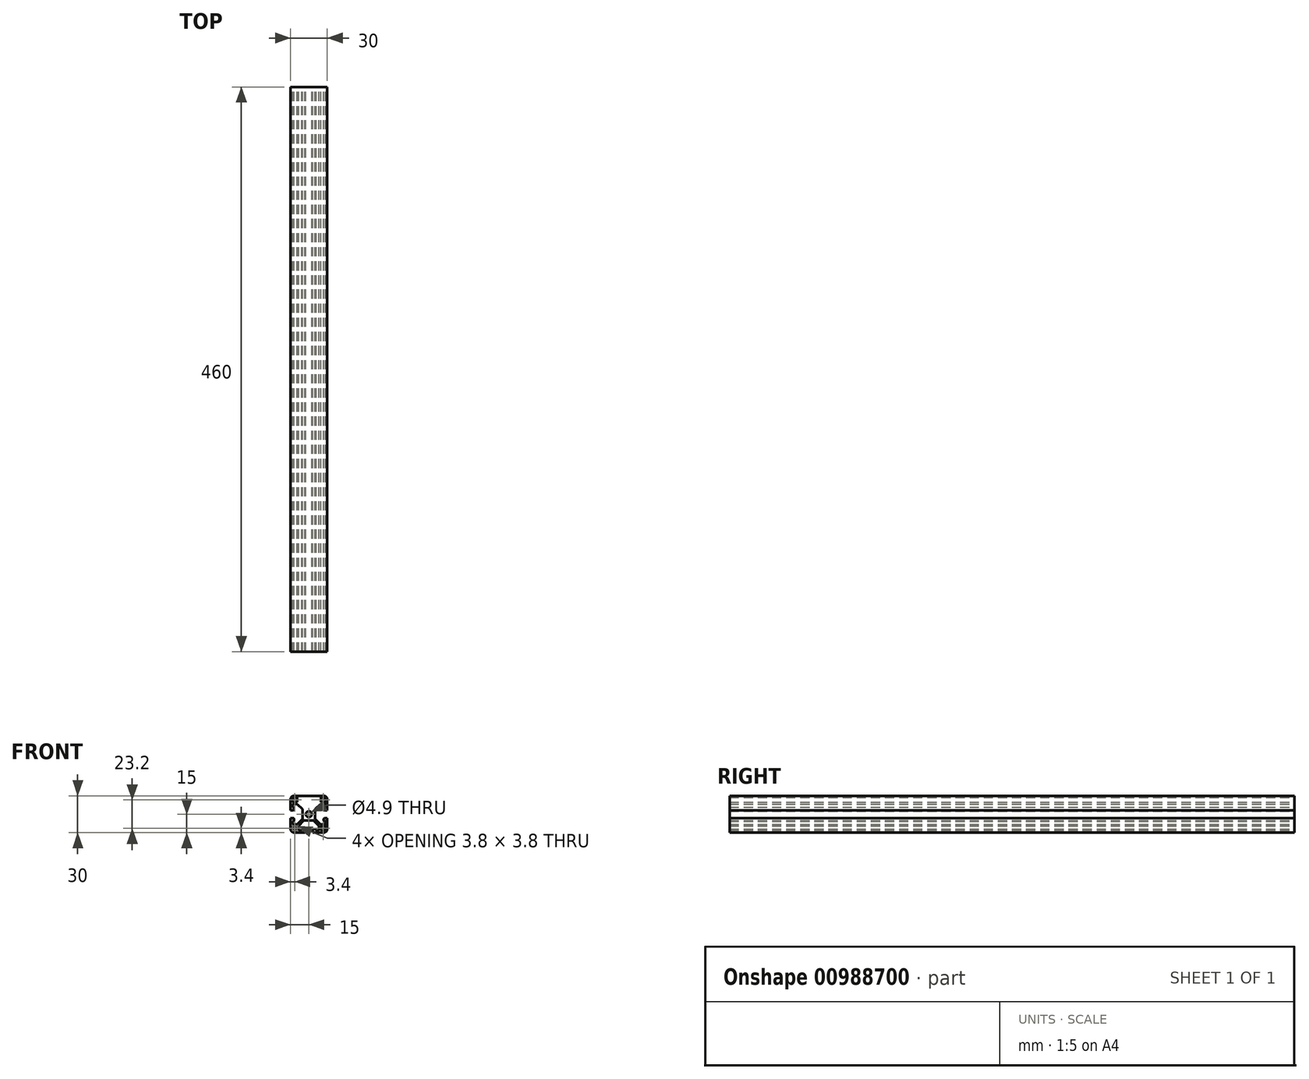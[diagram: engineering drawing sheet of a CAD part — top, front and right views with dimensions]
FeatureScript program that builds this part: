
annotation { "Feature Type Name" : "Feature", "Feature Type Description" : "" }
export const myFeature = defineFeature(function(context is Context, id is Id, definition is map)
    precondition{}
    {
        {
            var Q0;
            Q0=qCreatedBy(makeId("Front.planeOp"),FACE);
            var sketch = newSketch(context, id + "F0", { "sketchPlane" : qUnion([Q0])});
            skLineSegment(sketch, "E0.bottom", {"start": v(-12, 15) * mm, "end": v(12, 15) * mm});
            skLineSegment(sketch, "E0.top", {"start": v(-12, -15) * mm, "end": v(12, -15) * mm});
            skLineSegment(sketch, "E0.left", {"start": v(-15, 12) * mm, "end": v(-15, -12) * mm});
            skLineSegment(sketch, "E0.right", {"start": v(15, 12) * mm, "end": v(15, -12) * mm});
            skPoint(sketch, "E1.visualSharp", {"position": v(-15, 15) * mm});
            skArc(sketch, "E1.filletArc", {"start": v(-12, 15) * mm, "mid": v(-14.12, 14.12) * mm, "end": v(-15, 12) * mm});
            skPoint(sketch, "E2.visualSharp", {"position": v(15, 15) * mm});
            skArc(sketch, "E2.filletArc", {"start": v(15, 12) * mm, "mid": v(14.12, 14.12) * mm, "end": v(12, 15) * mm});
            skPoint(sketch, "E3.visualSharp", {"position": v(15, -15) * mm});
            skArc(sketch, "E3.filletArc", {"start": v(12, -15) * mm, "mid": v(14.12, -14.12) * mm, "end": v(15, -12) * mm});
            skPoint(sketch, "E4.visualSharp", {"position": v(-15, -15) * mm});
            skArc(sketch, "E4.filletArc", {"start": v(-15, -12) * mm, "mid": v(-14.12, -14.12) * mm, "end": v(-12, -15) * mm});
            skCircle(sketch, "E5", {"center": v(0, 0) * mm, "radius": 2.45 * mm});
            skPoint(sketch, "E6", {"position": v(15, 8.22) * mm});
            skPoint(sketch, "E7", {"position": v(15, -8.22) * mm});
            skPoint(sketch, "E8", {"position": v(15, 3.17) * mm});
            skPoint(sketch, "E9", {"position": v(15, -3.18) * mm});
            skLineSegment(sketch, "E10", {"start": v(15, 3.17) * mm, "end": v(13.09, 3.17) * mm});
            skLineSegment(sketch, "E11", {"start": v(13.09, -3.18) * mm, "end": v(15, -3.18) * mm});
            skPoint(sketch, "E12", {"position": v(12.06, -5.83) * mm});
            skPoint(sketch, "E13", {"position": v(12.06, 5.82) * mm});
            skPoint(sketch, "E14", {"position": v(13.5, -5.82) * mm});
            skPoint(sketch, "E15", {"position": v(13.5, 5.82) * mm});
            skPoint(sketch, "E16", {"position": v(13.5, 8.22) * mm});
            skPoint(sketch, "E17", {"position": v(13.5, -8.22) * mm});
            skPoint(sketch, "E18", {"position": v(9.5, 8.22) * mm});
            skPoint(sketch, "E19", {"position": v(9.5, -8.22) * mm});
            skPoint(sketch, "E20", {"position": v(5.1, -3.92) * mm});
            skPoint(sketch, "E21", {"position": v(5.1, 4.08) * mm});
            skLineSegment(sketch, "E22", {"start": v(12.09, -4.16) * mm, "end": v(12.08, -4.81) * mm});
            skLineSegment(sketch, "E23", {"start": v(13.5, -5.82) * mm, "end": v(13.5, -8.22) * mm});
            skLineSegment(sketch, "E24", {"start": v(9.2, -7.94) * mm, "end": v(5.4, -4.21) * mm});
            skLineSegment(sketch, "E25", {"start": v(5.1, 3.65) * mm, "end": v(5.1, -3.5) * mm});
            skLineSegment(sketch, "E26", {"start": v(5.41, 4.38) * mm, "end": v(9.21, 7.95) * mm});
            skLineSegment(sketch, "E27", {"start": v(13.5, 8.22) * mm, "end": v(9.9, 8.22) * mm});
            skLineSegment(sketch, "E28", {"start": v(13.5, 8.22) * mm, "end": v(13.5, 5.82) * mm});
            skLineSegment(sketch, "E29", {"start": v(13.08, 5.82) * mm, "end": v(13.5, 5.82) * mm});
            skLineSegment(sketch, "E30", {"start": v(12.08, 4.81) * mm, "end": v(12.09, 4.16) * mm});
            skLineSegment(sketch, "E31", {"start": v(13.08, -5.83) * mm, "end": v(13.5, -5.83) * mm});
            skLineSegment(sketch, "E32", {"start": v(13.5, -8.22) * mm, "end": v(9.9, -8.22) * mm});
            skLineSegment(sketch, "E33", {"start": v(13.5, -8.22) * mm, "end": v(13.5, -5.82) * mm});
            skArc(sketch, "E34.filletArc", {"start": v(9.9, 8.22) * mm, "mid": v(9.53, 8.15) * mm, "end": v(9.21, 7.95) * mm});
            skArc(sketch, "E35.filletArc", {"start": v(5.41, 4.38) * mm, "mid": v(5.18, 4.04) * mm, "end": v(5.1, 3.65) * mm});
            skArc(sketch, "E36.filletArc", {"start": v(5.1, -3.5) * mm, "mid": v(5.18, -3.89) * mm, "end": v(5.4, -4.21) * mm});
            skArc(sketch, "E37.filletArc", {"start": v(9.2, -7.94) * mm, "mid": v(9.53, -8.15) * mm, "end": v(9.9, -8.22) * mm});
            skArc(sketch, "E38.filletArc", {"start": v(12.08, -4.81) * mm, "mid": v(12.36, -5.53) * mm, "end": v(13.08, -5.83) * mm});
            skPoint(sketch, "E39.visualSharp", {"position": v(12.1, -3.18) * mm});
            skArc(sketch, "E39.filletArc", {"start": v(13.09, -3.18) * mm, "mid": v(12.38, -3.46) * mm, "end": v(12.09, -4.16) * mm});
            skPoint(sketch, "E40.visualSharp", {"position": v(12.1, 3.17) * mm});
            skArc(sketch, "E40.filletArc", {"start": v(12.09, 4.16) * mm, "mid": v(12.38, 3.46) * mm, "end": v(13.09, 3.17) * mm});
            skArc(sketch, "E41.filletArc", {"start": v(13.08, 5.82) * mm, "mid": v(12.36, 5.53) * mm, "end": v(12.08, 4.81) * mm});
            skArc(sketch, "E42.MirrorCS", {"start": v(-5.1, -3.5) * mm, "mid": v(-5.18, -3.89) * mm, "end": v(-5.4, -4.21) * mm});
            skLineSegment(sketch, "E43.MirrorCS", {"start": v(-13.08, -5.83) * mm, "end": v(-13.5, -5.83) * mm});
            skArc(sketch, "E44.MirrorCS", {"start": v(-9.2, -7.94) * mm, "mid": v(-9.53, -8.15) * mm, "end": v(-9.9, -8.22) * mm});
            skLineSegment(sketch, "E45.MirrorCS", {"start": v(-13.08, 5.82) * mm, "end": v(-13.5, 5.82) * mm});
            skArc(sketch, "E46.MirrorCS", {"start": v(-5.41, 4.38) * mm, "mid": v(-5.18, 4.04) * mm, "end": v(-5.1, 3.65) * mm});
            skArc(sketch, "E47.MirrorCS", {"start": v(-9.9, 8.22) * mm, "mid": v(-9.53, 8.15) * mm, "end": v(-9.21, 7.95) * mm});
            skArc(sketch, "E48.MirrorCS", {"start": v(-13.08, 5.82) * mm, "mid": v(-12.36, 5.53) * mm, "end": v(-12.08, 4.81) * mm});
            skLineSegment(sketch, "E49.MirrorCS", {"start": v(-12.08, 4.81) * mm, "end": v(-12.09, 4.16) * mm});
            skLineSegment(sketch, "E50.MirrorCS", {"start": v(-12.09, -4.16) * mm, "end": v(-12.08, -4.81) * mm});
            skArc(sketch, "E51.MirrorCS", {"start": v(-12.08, -4.81) * mm, "mid": v(-12.36, -5.53) * mm, "end": v(-13.08, -5.83) * mm});
            skLineSegment(sketch, "E52.MirrorCS", {"start": v(-13.5, -8.22) * mm, "end": v(-13.5, -5.82) * mm});
            skLineSegment(sketch, "E53.MirrorCS", {"start": v(-13.5, -5.82) * mm, "end": v(-13.5, -8.22) * mm});
            skLineSegment(sketch, "E54.MirrorCS", {"start": v(-13.09, -3.18) * mm, "end": v(-15, -3.18) * mm});
            skArc(sketch, "E55.MirrorCS", {"start": v(-12.09, 4.16) * mm, "mid": v(-12.38, 3.46) * mm, "end": v(-13.09, 3.17) * mm});
            skArc(sketch, "E56.MirrorCS", {"start": v(-13.09, -3.18) * mm, "mid": v(-12.38, -3.46) * mm, "end": v(-12.09, -4.16) * mm});
            skLineSegment(sketch, "E57.MirrorCS", {"start": v(-15, 3.17) * mm, "end": v(-13.09, 3.17) * mm});
            skPoint(sketch, "E58.MirrorP", {"position": v(-5.1, -3.92) * mm});
            skPoint(sketch, "E59.MirrorP", {"position": v(-9.5, -8.22) * mm});
            skPoint(sketch, "E60.MirrorP", {"position": v(-13.5, -8.22) * mm});
            skPoint(sketch, "E61.MirrorP", {"position": v(-12.06, 5.82) * mm});
            skPoint(sketch, "E62.MirrorP", {"position": v(-5.1, 4.08) * mm});
            skLineSegment(sketch, "E63.MirrorCS", {"start": v(-13.5, 8.22) * mm, "end": v(-13.5, 5.82) * mm});
            skPoint(sketch, "E64.MirrorP", {"position": v(-12.06, -5.83) * mm});
            skPoint(sketch, "E65.MirrorP", {"position": v(-9.5, 8.22) * mm});
            skPoint(sketch, "E66.MirrorP", {"position": v(-15, 8.22) * mm});
            skPoint(sketch, "E67.MirrorP", {"position": v(-13.5, 5.82) * mm});
            skLineSegment(sketch, "E68.MirrorCS", {"start": v(-13.5, 8.22) * mm, "end": v(-9.9, 8.22) * mm});
            skPoint(sketch, "E69.MirrorP", {"position": v(-13.5, -5.82) * mm});
            skLineSegment(sketch, "E70.MirrorCS", {"start": v(-13.5, -8.22) * mm, "end": v(-9.9, -8.22) * mm});
            skLineSegment(sketch, "E71.MirrorCS", {"start": v(-5.1, 3.65) * mm, "end": v(-5.1, -3.5) * mm});
            skPoint(sketch, "E72.MirrorP", {"position": v(-13.5, 8.22) * mm});
            skPoint(sketch, "E73.MirrorP", {"position": v(-15, -3.18) * mm});
            skPoint(sketch, "E74.MirrorP", {"position": v(-12.1, 3.17) * mm});
            skPoint(sketch, "E75.MirrorP", {"position": v(-15, -8.22) * mm});
            skPoint(sketch, "E76.MirrorP", {"position": v(-12.1, -3.18) * mm});
            skLineSegment(sketch, "E77.MirrorCS", {"start": v(-5.41, 4.38) * mm, "end": v(-9.21, 7.95) * mm});
            skLineSegment(sketch, "E78.MirrorCS", {"start": v(-9.2, -7.94) * mm, "end": v(-5.4, -4.21) * mm});
            skPoint(sketch, "E79.MirrorP", {"position": v(-15, 3.17) * mm});
            skArc(sketch, "E80.MirrorCS", {"start": v(-3.5, 5.1) * mm, "mid": v(-3.89, 5.18) * mm, "end": v(-4.21, 5.4) * mm});
            skLineSegment(sketch, "E81.MirrorCS", {"start": v(-5.82, 13.08) * mm, "end": v(-5.82, 13.5) * mm});
            skArc(sketch, "E82.MirrorCS", {"start": v(-7.94, 9.2) * mm, "mid": v(-8.15, 9.53) * mm, "end": v(-8.22, 9.9) * mm});
            skLineSegment(sketch, "E83.MirrorCS", {"start": v(5.83, 13.08) * mm, "end": v(5.83, 13.5) * mm});
            skArc(sketch, "E84.MirrorCS", {"start": v(4.38, 5.41) * mm, "mid": v(4.04, 5.18) * mm, "end": v(3.65, 5.1) * mm});
            skArc(sketch, "E85.MirrorCS", {"start": v(8.23, 9.9) * mm, "mid": v(8.15, 9.53) * mm, "end": v(7.95, 9.21) * mm});
            skArc(sketch, "E86.MirrorCS", {"start": v(5.83, 13.08) * mm, "mid": v(5.53, 12.36) * mm, "end": v(4.81, 12.08) * mm});
            skLineSegment(sketch, "E87.MirrorCS", {"start": v(4.81, 12.08) * mm, "end": v(4.16, 12.09) * mm});
            skLineSegment(sketch, "E88.MirrorCS", {"start": v(-4.16, 12.09) * mm, "end": v(-4.81, 12.08) * mm});
            skArc(sketch, "E89.MirrorCS", {"start": v(-4.81, 12.08) * mm, "mid": v(-5.53, 12.36) * mm, "end": v(-5.82, 13.08) * mm});
            skLineSegment(sketch, "E90.MirrorCS", {"start": v(-8.22, 13.5) * mm, "end": v(-5.82, 13.5) * mm});
            skLineSegment(sketch, "E91.MirrorCS", {"start": v(-5.82, 13.5) * mm, "end": v(-8.22, 13.5) * mm});
            skLineSegment(sketch, "E92.MirrorCS", {"start": v(-3.17, 13.09) * mm, "end": v(-3.17, 15) * mm});
            skArc(sketch, "E93.MirrorCS", {"start": v(4.16, 12.09) * mm, "mid": v(3.46, 12.38) * mm, "end": v(3.18, 13.09) * mm});
            skArc(sketch, "E94.MirrorCS", {"start": v(-3.17, 13.09) * mm, "mid": v(-3.46, 12.38) * mm, "end": v(-4.16, 12.09) * mm});
            skLineSegment(sketch, "E95.MirrorCS", {"start": v(3.18, 15) * mm, "end": v(3.18, 13.09) * mm});
            skPoint(sketch, "E96.MirrorP", {"position": v(-3.92, 5.1) * mm});
            skPoint(sketch, "E97.MirrorP", {"position": v(-8.22, 9.5) * mm});
            skPoint(sketch, "E98.MirrorP", {"position": v(-8.22, 13.5) * mm});
            skPoint(sketch, "E99.MirrorP", {"position": v(5.83, 12.06) * mm});
            skPoint(sketch, "E100.MirrorP", {"position": v(4.08, 5.1) * mm});
            skLineSegment(sketch, "E101.MirrorCS", {"start": v(8.23, 13.5) * mm, "end": v(5.83, 13.5) * mm});
            skPoint(sketch, "E102.MirrorP", {"position": v(-5.82, 12.06) * mm});
            skPoint(sketch, "E103.MirrorP", {"position": v(8.23, 9.5) * mm});
            skPoint(sketch, "E104.MirrorP", {"position": v(8.23, 15) * mm});
            skPoint(sketch, "E105.MirrorP", {"position": v(5.83, 13.5) * mm});
            skLineSegment(sketch, "E106.MirrorCS", {"start": v(8.23, 13.5) * mm, "end": v(8.23, 9.9) * mm});
            skPoint(sketch, "E107.MirrorP", {"position": v(-5.82, 13.5) * mm});
            skLineSegment(sketch, "E108.MirrorCS", {"start": v(-8.22, 13.5) * mm, "end": v(-8.22, 9.9) * mm});
            skLineSegment(sketch, "E109.MirrorCS", {"start": v(3.65, 5.1) * mm, "end": v(-3.5, 5.1) * mm});
            skPoint(sketch, "E110.MirrorP", {"position": v(8.23, 13.5) * mm});
            skPoint(sketch, "E111.MirrorP", {"position": v(-3.17, 15) * mm});
            skPoint(sketch, "E112.MirrorP", {"position": v(3.18, 12.1) * mm});
            skPoint(sketch, "E113.MirrorP", {"position": v(-8.22, 15) * mm});
            skPoint(sketch, "E114.MirrorP", {"position": v(-3.17, 12.1) * mm});
            skLineSegment(sketch, "E115.MirrorCS", {"start": v(4.38, 5.41) * mm, "end": v(7.95, 9.21) * mm});
            skLineSegment(sketch, "E116.MirrorCS", {"start": v(-7.94, 9.2) * mm, "end": v(-4.21, 5.4) * mm});
            skPoint(sketch, "E117.MirrorP", {"position": v(3.18, 15) * mm});
            skPoint(sketch, "E118", {"position": v(-8.22, -15) * mm});
            skArc(sketch, "E119.MirrorCS", {"start": v(3.5, -5.1) * mm, "mid": v(3.89, -5.18) * mm, "end": v(4.21, -5.4) * mm});
            skLineSegment(sketch, "E120.MirrorCS", {"start": v(5.83, -13.08) * mm, "end": v(5.83, -13.5) * mm});
            skArc(sketch, "E121.MirrorCS", {"start": v(7.94, -9.2) * mm, "mid": v(8.15, -9.53) * mm, "end": v(8.23, -9.9) * mm});
            skLineSegment(sketch, "E122.MirrorCS", {"start": v(-5.82, -13.08) * mm, "end": v(-5.82, -13.5) * mm});
            skArc(sketch, "E123.MirrorCS", {"start": v(-4.38, -5.41) * mm, "mid": v(-4.04, -5.18) * mm, "end": v(-3.65, -5.1) * mm});
            skArc(sketch, "E124.MirrorCS", {"start": v(-8.22, -9.9) * mm, "mid": v(-8.15, -9.53) * mm, "end": v(-7.95, -9.21) * mm});
            skArc(sketch, "E125.MirrorCS", {"start": v(-5.82, -13.08) * mm, "mid": v(-5.53, -12.36) * mm, "end": v(-4.81, -12.08) * mm});
            skLineSegment(sketch, "E126.MirrorCS", {"start": v(-4.81, -12.08) * mm, "end": v(-4.16, -12.09) * mm});
            skLineSegment(sketch, "E127.MirrorCS", {"start": v(4.16, -12.09) * mm, "end": v(4.81, -12.08) * mm});
            skArc(sketch, "E128.MirrorCS", {"start": v(4.81, -12.08) * mm, "mid": v(5.53, -12.36) * mm, "end": v(5.83, -13.08) * mm});
            skLineSegment(sketch, "E129.MirrorCS", {"start": v(8.23, -13.5) * mm, "end": v(5.83, -13.5) * mm});
            skLineSegment(sketch, "E130.MirrorCS", {"start": v(5.83, -13.5) * mm, "end": v(8.23, -13.5) * mm});
            skLineSegment(sketch, "E131.MirrorCS", {"start": v(3.18, -13.09) * mm, "end": v(3.18, -15) * mm});
            skArc(sketch, "E132.MirrorCS", {"start": v(-4.16, -12.09) * mm, "mid": v(-3.46, -12.38) * mm, "end": v(-3.17, -13.09) * mm});
            skArc(sketch, "E133.MirrorCS", {"start": v(3.18, -13.09) * mm, "mid": v(3.46, -12.38) * mm, "end": v(4.16, -12.09) * mm});
            skLineSegment(sketch, "E134.MirrorCS", {"start": v(-3.17, -15) * mm, "end": v(-3.17, -13.09) * mm});
            skPoint(sketch, "E135.MirrorP", {"position": v(3.92, -5.1) * mm});
            skPoint(sketch, "E136.MirrorP", {"position": v(8.23, -9.5) * mm});
            skPoint(sketch, "E137.MirrorP", {"position": v(8.23, -13.5) * mm});
            skPoint(sketch, "E138.MirrorP", {"position": v(-5.82, -12.06) * mm});
            skPoint(sketch, "E139.MirrorP", {"position": v(-4.08, -5.1) * mm});
            skLineSegment(sketch, "E140.MirrorCS", {"start": v(-8.22, -13.5) * mm, "end": v(-5.82, -13.5) * mm});
            skPoint(sketch, "E141.MirrorP", {"position": v(5.83, -12.06) * mm});
            skPoint(sketch, "E142.MirrorP", {"position": v(-8.22, -9.5) * mm});
            skPoint(sketch, "E143.MirrorP", {"position": v(-5.82, -13.5) * mm});
            skLineSegment(sketch, "E144.MirrorCS", {"start": v(-8.22, -13.5) * mm, "end": v(-8.22, -9.9) * mm});
            skPoint(sketch, "E145.MirrorP", {"position": v(5.83, -13.5) * mm});
            skLineSegment(sketch, "E146.MirrorCS", {"start": v(8.23, -13.5) * mm, "end": v(8.23, -9.9) * mm});
            skLineSegment(sketch, "E147.MirrorCS", {"start": v(-3.65, -5.1) * mm, "end": v(3.5, -5.1) * mm});
            skPoint(sketch, "E148.MirrorP", {"position": v(-8.22, -13.5) * mm});
            skPoint(sketch, "E149.MirrorP", {"position": v(3.18, -15) * mm});
            skPoint(sketch, "E150.MirrorP", {"position": v(-3.17, -12.1) * mm});
            skPoint(sketch, "E151.MirrorP", {"position": v(8.23, -15) * mm});
            skPoint(sketch, "E152.MirrorP", {"position": v(3.18, -12.1) * mm});
            skLineSegment(sketch, "E153.MirrorCS", {"start": v(-4.38, -5.41) * mm, "end": v(-7.95, -9.21) * mm});
            skLineSegment(sketch, "E154.MirrorCS", {"start": v(7.94, -9.2) * mm, "end": v(4.21, -5.4) * mm});
            skPoint(sketch, "E155.MirrorP", {"position": v(-3.17, -15) * mm});
            skLineSegment(sketch, "E156.bottom", {"start": v(-13.5, -9.7) * mm, "end": v(-9.7, -9.7) * mm});
            skLineSegment(sketch, "E156.top", {"start": v(-11.5, -13.5) * mm, "end": v(-9.7, -13.5) * mm});
            skLineSegment(sketch, "E156.left", {"start": v(-13.5, -9.7) * mm, "end": v(-13.5, -11.5) * mm});
            skLineSegment(sketch, "E156.right", {"start": v(-9.7, -9.7) * mm, "end": v(-9.7, -13.5) * mm});
            skPoint(sketch, "E157.visualSharp", {"position": v(-13.5, -13.5) * mm});
            skArc(sketch, "E157.filletArc", {"start": v(-13.5, -11.5) * mm, "mid": v(-12.91, -12.91) * mm, "end": v(-11.5, -13.5) * mm});
            skPoint(sketch, "E158", {"position": v(-11.6, -11.6) * mm});
            skPoint(sketch, "E159.MirrorP", {"position": v(-11.6, 11.6) * mm});
            skLineSegment(sketch, "E160.MirrorCS", {"start": v(-11.5, 13.5) * mm, "end": v(-9.7, 13.5) * mm});
            skLineSegment(sketch, "E161.MirrorCS", {"start": v(-9.7, 9.7) * mm, "end": v(-9.7, 13.5) * mm});
            skLineSegment(sketch, "E162.MirrorCS", {"start": v(-13.5, 9.7) * mm, "end": v(-9.7, 9.7) * mm});
            skLineSegment(sketch, "E163.MirrorCS", {"start": v(-13.5, 9.7) * mm, "end": v(-13.5, 11.5) * mm});
            skPoint(sketch, "E164.MirrorP", {"position": v(-13.5, 13.5) * mm});
            skArc(sketch, "E165.MirrorCS", {"start": v(-13.5, 11.5) * mm, "mid": v(-12.91, 12.91) * mm, "end": v(-11.5, 13.5) * mm});
            skPoint(sketch, "E166.MirrorP", {"position": v(11.6, 11.6) * mm});
            skLineSegment(sketch, "E167.MirrorCS", {"start": v(11.5, 13.5) * mm, "end": v(9.7, 13.5) * mm});
            skLineSegment(sketch, "E168.MirrorCS", {"start": v(13.5, 9.7) * mm, "end": v(9.7, 9.7) * mm});
            skLineSegment(sketch, "E169.MirrorCS", {"start": v(9.7, 9.7) * mm, "end": v(9.7, 13.5) * mm});
            skLineSegment(sketch, "E170.MirrorCS", {"start": v(13.5, 9.7) * mm, "end": v(13.5, 11.5) * mm});
            skArc(sketch, "E171.MirrorCS", {"start": v(13.5, 11.5) * mm, "mid": v(12.91, 12.91) * mm, "end": v(11.5, 13.5) * mm});
            skPoint(sketch, "E172.MirrorP", {"position": v(11.6, -11.6) * mm});
            skLineSegment(sketch, "E173.MirrorCS", {"start": v(13.5, -9.7) * mm, "end": v(13.5, -11.5) * mm});
            skArc(sketch, "E174.MirrorCS", {"start": v(13.5, -11.5) * mm, "mid": v(12.91, -12.91) * mm, "end": v(11.5, -13.5) * mm});
            skLineSegment(sketch, "E175.MirrorCS", {"start": v(13.5, -9.7) * mm, "end": v(9.7, -9.7) * mm});
            skLineSegment(sketch, "E176.MirrorCS", {"start": v(9.7, -9.7) * mm, "end": v(9.7, -13.5) * mm});
            skLineSegment(sketch, "E177.MirrorCS", {"start": v(11.5, -13.5) * mm, "end": v(9.7, -13.5) * mm});
            skSolve(sketch);
        }
        {
            var Q0;
            {var subQ13=sQuery(id+"F0.wireOp",EDGE,"E1.filletArc");Q0=makeQuery(id+"F0.imprint","IMPRINT",FACE,{"disambiguationData":[TD([[makeQuery(id+"F0.imprint","IMPRINT",EDGE,{"derivedFrom":subQ13}),1.0]])]});}
            extrude(context, id + "F1", {"entities" : qUnion([Q0]), "depth" : 460 * mm, "offsetDistance" : 25 * mm});
        }
    });
